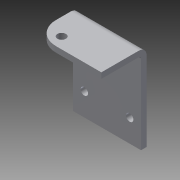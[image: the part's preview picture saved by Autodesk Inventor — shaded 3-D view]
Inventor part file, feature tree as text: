
AUTODESK INVENTOR PART (.ipt)
format: ipt  version: 2014 (Build 180170000, 170)  size: 119,808 bytes
history: native  units: in
note: dims shown in document units (in); Inventor stores cm internally (conversion verified against a paired STEP export)
features: sheet_metal_op x4, sketch x3, other x3
ambient origin geometry x8: Origin, YZ Plane, XZ Plane, XY Plane, X Axis, Y Axis, Z Axis, Center Point
bodies: Solid1 (feature_tree)
feature tree (10):
  sheet_metal_op  "Face1"
  sheet_metal_op  "Flange1"
  sketch  "Sketch1"  dims[d0=1.5in]
  other  "Plate1"
  sketch  "Sketch2"  dims[d1=1.75in]
  other  "Plate2"
  sheet_metal_op  "Bend1"
  sheet_metal_op  "Corner1"
  sketch  "Sketch4"  dims[d2=0.163in d3=0.25in d4=0.7874in d6=1.0in d7=0.3937in d9=1.0in d11=0.125in d12=0.125in d13=0.0625in d14=0.25in d15=0.125in d16=1.0in d17=90.0deg d18=0.05in d19=0.5in d20=0.125in d21=0.125in d22=0.5in d28=0.187in d29=0.25in d31=0.125in d32=0.0in d34=0.375in d35=0.5in]
  other  "Cut2"
